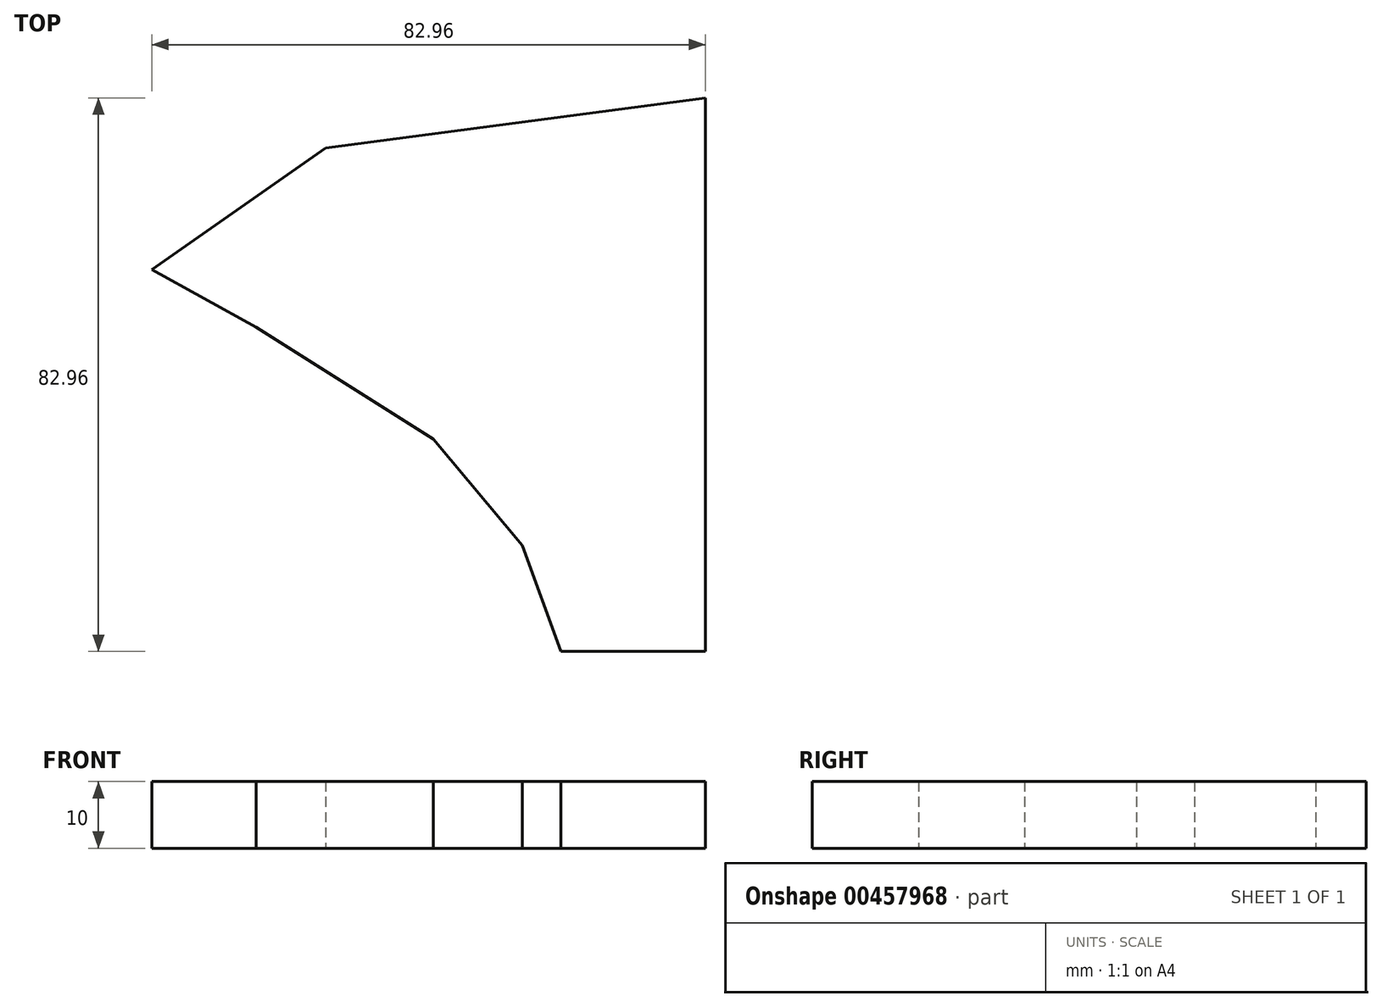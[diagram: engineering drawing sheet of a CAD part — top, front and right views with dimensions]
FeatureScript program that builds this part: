
annotation { "Feature Type Name" : "Feature", "Feature Type Description" : "" }
export const myFeature = defineFeature(function(context is Context, id is Id, definition is map)
    precondition{}
    {
        {
            var Q0;
            Q0=qCreatedBy(makeId("Top.planeOp"),FACE);
            var sketch = newSketch(context, id + "F0", { "sketchPlane" : qUnion([Q0])});
            skLineSegment(sketch, "E0", {"start": v(7.23, 56.08) * mm, "end": v(64.17, 63.6) * mm});
            skLineSegment(sketch, "E1", {"start": v(64.17, 63.6) * mm, "end": v(64.17, -19.37) * mm});
            skLineSegment(sketch, "E2", {"start": v(64.17, -19.37) * mm, "end": v(42.5, -19.37) * mm});
            skLineSegment(sketch, "E3", {"start": v(42.5, -19.37) * mm, "end": v(36.71, -3.47) * mm});
            skLineSegment(sketch, "E4", {"start": v(36.71, -3.47) * mm, "end": v(23.41, 12.43) * mm});
            skLineSegment(sketch, "E5", {"start": v(23.41, 12.43) * mm, "end": v(-3.18, 29.2) * mm});
            skLineSegment(sketch, "E6", {"start": v(-3.18, 29.2) * mm, "end": v(-18.79, 37.87) * mm});
            skLineSegment(sketch, "E7", {"start": v(-18.79, 37.87) * mm, "end": v(7.23, 56.08) * mm});
            skSolve(sketch);
        }
        {
            var Q0;
            Q0=makeQuery(id+"F0.imprint","IMPRINT",FACE,{"disambiguationData":[TD([[makeQuery(id+"F0.imprint","IMPRINT",EDGE,{"derivedFrom":sQuery(id+"F0.wireOp",EDGE,"E0")}),-1.0]])]});
            extrude(context, id + "F1", {"entities" : qUnion([Q0]), "depth" : 10 * mm});
        }
    });
